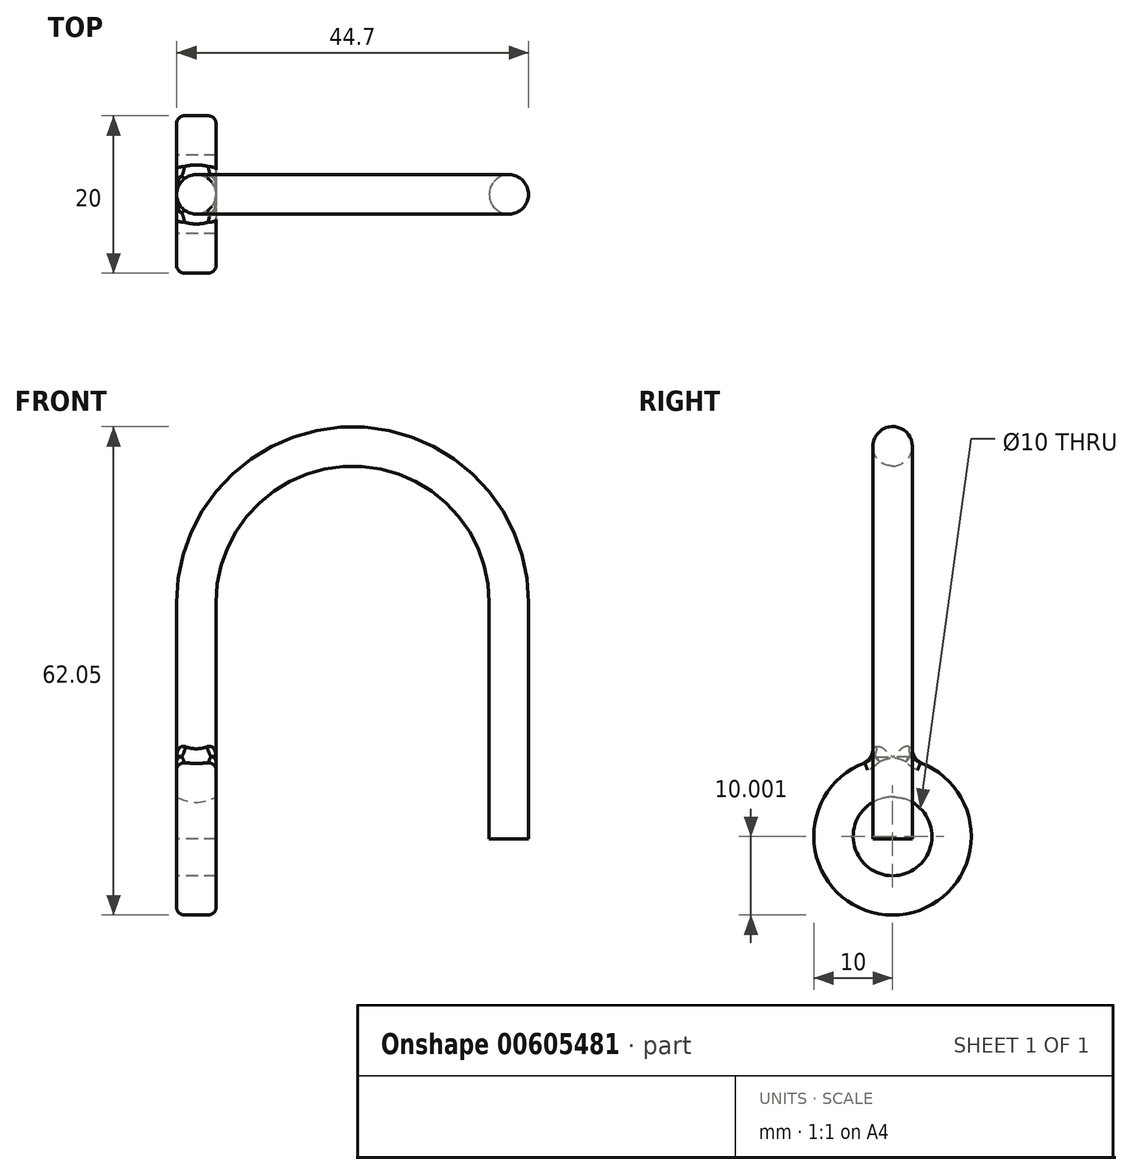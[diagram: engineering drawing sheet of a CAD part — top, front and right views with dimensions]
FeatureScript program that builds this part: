
annotation { "Feature Type Name" : "Feature", "Feature Type Description" : "" }
export const myFeature = defineFeature(function(context is Context, id is Id, definition is map)
    precondition{}
    {
        {
            var Q0;
            Q0=qCreatedBy(makeId("Front.planeOp"),FACE);
            var sketch = newSketch(context, id + "F0", { "sketchPlane" : qUnion([Q0])});
            skLineSegment(sketch, "E0", {"start": v(-22.85, -1.07) * mm, "end": v(-22.85, 28.93) * mm});
            skLineSegment(sketch, "E1", {"start": v(-2.85, 48.93) * mm, "end": v(-2.85, 48.93) * mm});
            skLineSegment(sketch, "E2", {"start": v(17.15, 28.93) * mm, "end": v(17.15, -1.07) * mm});
            skPoint(sketch, "E3.visualSharp", {"position": v(-22.85, 48.93) * mm});
            skArc(sketch, "E3.filletArc", {"start": v(-2.85, 48.93) * mm, "mid": v(-17, 43.07) * mm, "end": v(-22.85, 28.93) * mm});
            skPoint(sketch, "E4.visualSharp", {"position": v(17.15, 48.93) * mm});
            skArc(sketch, "E4.filletArc", {"start": v(17.15, 28.93) * mm, "mid": v(11.3, 43.07) * mm, "end": v(-2.85, 48.93) * mm});
            skLineSegment(sketch, "E5", {"start": v(-47.25, -1.07) * mm, "end": v(36.5, -1.07) * mm, "construction": true});
            skSolve(sketch);
        }
        {
            var Q0;
            Q0=sQuery(id+"F0.wireOp",VERTEX,"E0.start");
            var Q1;
            Q1=sQuery(id+"F0.wireOp",EDGE,"E0");
            cPlane(context, id + "F1", {"entities" : qUnion([Q0, Q1]), "cplaneType" : CPlaneType.LINE_POINT, "offset" : 25 * mm, "width" : 150 * mm, "height" : 150 * mm});
        }
        {
            var Q0;
            Q0=qCreatedBy(id+"F1.planeOp",FACE);
            var sketch = newSketch(context, id + "F2", { "sketchPlane" : qUnion([Q0])});
            skCircle(sketch, "E6", {"center": v(-22.7, 0) * mm, "radius": 2.5 * mm});
            skSolve(sketch);
        }
        {
            var Q0;
            Q0=sQuery(id+"F2.wireOp",VERTEX,"E6.center");
            var Q1;
            Q1=sQuery(id+"F0.wireOp",EDGE,"E5");
            cPlane(context, id + "F3", {"entities" : qUnion([Q0, Q1]), "cplaneType" : CPlaneType.LINE_POINT, "offset" : 25 * mm, "width" : 150 * mm, "height" : 150 * mm});
        }
        {
            var Q0;
            Q0=makeQuery(id+"F2.imprint","IMPRINT",FACE,{"disambiguationData":[TD([[makeQuery(id+"F2.imprint","IMPRINT",EDGE,{"derivedFrom":sQuery(id+"F2.wireOp",EDGE,"E6")}),1.0]])]});
            var Q1;
            Q1 = qConstructionFilter(qBodyType(qCreatedBy(id + "F0" ,EDGE), BodyType.WIRE), ConstructionObject.NO);
            sweep(context, id + "F4", {"profiles" : qUnion([Q0]), "path" : qUnion([Q1])});
        }
        {
            var Q0;
            Q0=qCreatedBy(id+"F3.planeOp",FACE);
            var sketch = newSketch(context, id + "F5", { "sketchPlane" : qUnion([Q0])});
            skCircle(sketch, "E7", {"center": v(0, -0.77) * mm, "radius": 10 * mm});
            skCircle(sketch, "E8", {"center": v(0, -0.77) * mm, "radius": 5 * mm});
            skSolve(sketch);
        }
        {
            var Q0;
            Q0=makeQuery(id+"F5.imprint","IMPRINT",FACE,{"disambiguationData":[TD([[makeQuery(id+"F5.imprint","IMPRINT",EDGE,{"derivedFrom":sQuery(id+"F5.wireOp",EDGE,"E7")}),1.0]])]});
            extrude(context, id + "F6", {"entities" : qUnion([Q0]), "operationType" : NewBodyOperationType.ADD, "depth" : 5 * mm, "offsetDistance" : 25 * mm, "symmetric" : true});
        }
        {
            var Q0;
            Q0=makeQuery(id+"F6.boolean.opBoolean","INTERSECT",EDGE,{"disambiguationData":[OD(1.0)],"derivedFrom":[makeQuery(id+"F4.opSweep","SWEPT_FACE",FACE,{"disambiguationData":[OSD([sQuery(id+"F0.wireOp",EDGE,"E0"),sQuery(id+"F2.wireOp",EDGE,"E6")])]}),makeQuery(id+"F6.opExtrude","SWEPT_FACE",FACE,{"disambiguationData":[OSD([sQuery(id+"F5.wireOp",EDGE,"E7")])]})]});
            fillet(context, id + "F7", {"entities" : qUnion([Q0]), "radius" : 2 * mm, "tangentPropagation" : true, "allowEdgeOverflow" : false});
        }
        {
            var Q0;
            Q0=makeQuery(id+"F6.opExtrude","CAP_EDGE",EDGE,{"disambiguationData":[OSD([sQuery(id+"F5.wireOp",EDGE,"E7")])],"isStart":true});
            var Q1;
            Q1=makeQuery(id+"F6.opExtrude","CAP_EDGE",EDGE,{"disambiguationData":[OSD([sQuery(id+"F5.wireOp",EDGE,"E7")])],"isStart":false});
            fillet(context, id + "F8", {"entities" : qUnion([Q0, Q1]), "radius" : 1 * mm, "tangentPropagation" : true, "allowEdgeOverflow" : false});
        }
    });
